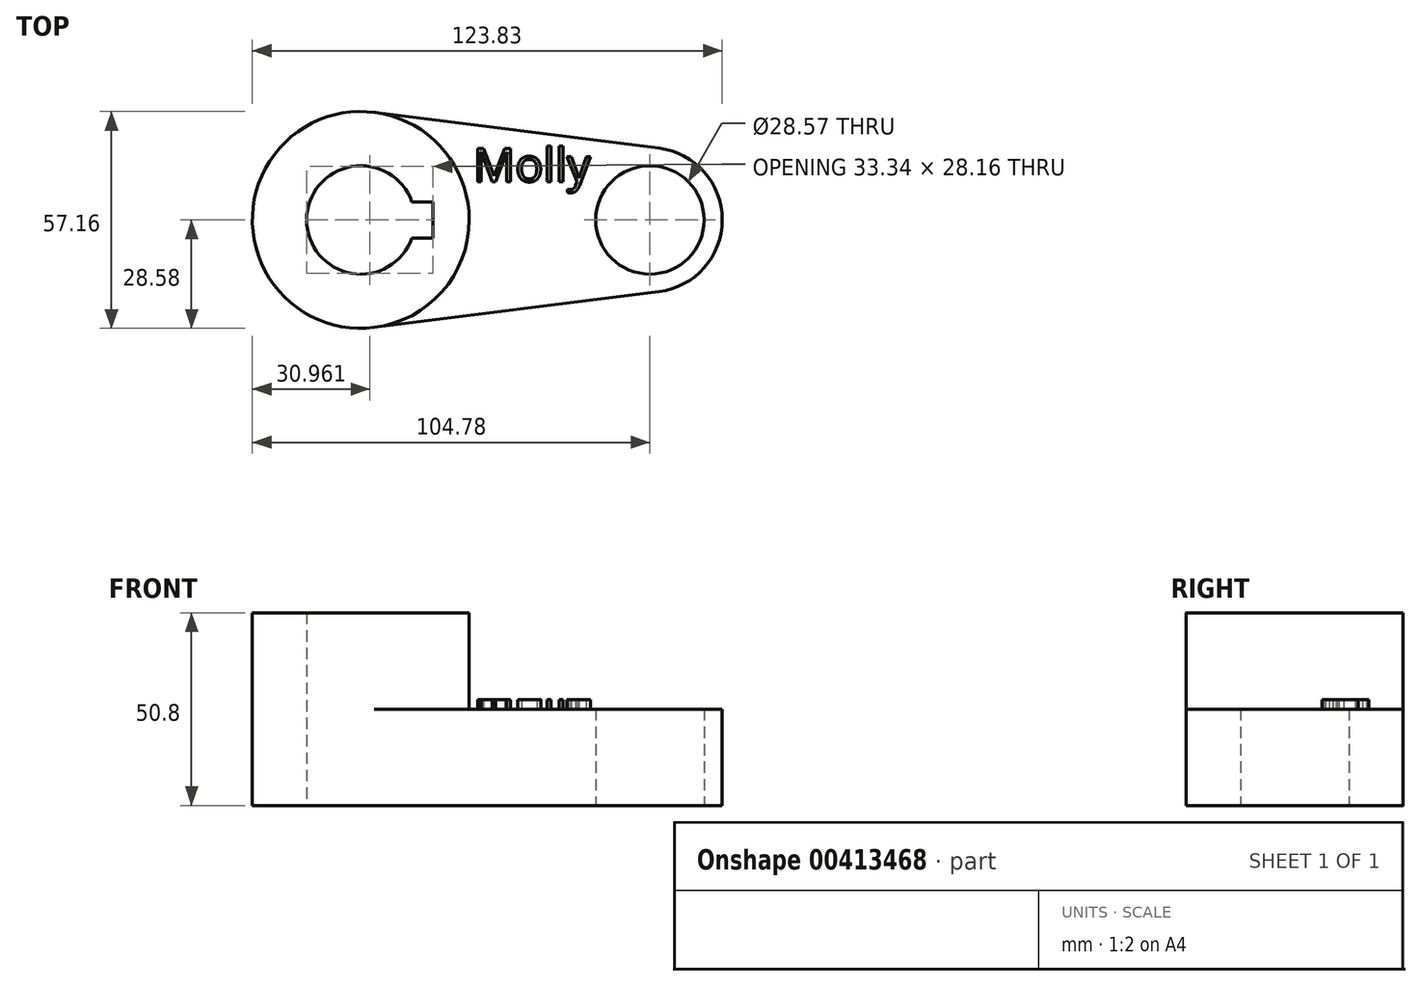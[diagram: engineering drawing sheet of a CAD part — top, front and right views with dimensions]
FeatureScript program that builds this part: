
annotation { "Feature Type Name" : "Feature", "Feature Type Description" : "" }
export const myFeature = defineFeature(function(context is Context, id is Id, definition is map)
    precondition{}
    {
        {
            var Q0;
            Q0=qCreatedBy(makeId("Top.planeOp"),FACE);
            var sketch = newSketch(context, id + "F0", { "sketchPlane" : qUnion([Q0])});
            skCircle(sketch, "E0", {"center": v(0, 0) * mm, "radius": 28.58 * mm});
            skCircle(sketch, "E1", {"center": v(76.2, 0) * mm, "radius": 19.05 * mm});
            skLineSegment(sketch, "E2", {"start": v(3.57, 28.35) * mm, "end": v(78.58, 18.9) * mm});
            skLineSegment(sketch, "E3", {"start": v(3.57, -28.35) * mm, "end": v(78.58, -18.9) * mm});
            skCircle(sketch, "E4", {"center": v(0, 0) * mm, "radius": 14.29 * mm});
            skCircle(sketch, "E5", {"center": v(76.2, 0) * mm, "radius": 14.29 * mm});
            skLineSegment(sketch, "E6.bottom", {"start": v(-19.05, -4.76) * mm, "end": v(19.05, -4.76) * mm});
            skLineSegment(sketch, "E6.top", {"start": v(-19.05, 4.76) * mm, "end": v(19.05, 4.76) * mm});
            skLineSegment(sketch, "E6.left", {"start": v(-19.05, -4.76) * mm, "end": v(-19.05, 4.76) * mm});
            skLineSegment(sketch, "E6.right", {"start": v(19.05, -4.76) * mm, "end": v(19.05, 4.76) * mm});
            skSolve(sketch);
        }
        {
            var Q0;
            {var subQ7=sQuery(id+"F0.wireOp",EDGE,"E6.left");Q0=makeQuery(id+"F0.imprint","IMPRINT",FACE,{"disambiguationData":[TD([[makeQuery(id+"F0.imprint","IMPRINT",EDGE,{"derivedFrom":subQ7}),1.0]])]});}
            var Q1;
            {var subQ5=sQuery(id+"F0.wireOp",EDGE,"E6.left");Q1=makeQuery(id+"F0.imprint","IMPRINT",FACE,{"disambiguationData":[TD([[makeQuery(id+"F0.imprint","IMPRINT",EDGE,{"derivedFrom":subQ5}),-1.0]])]});}
            var Q2;
            {var subQ0=sQuery(id+"F0.wireOp",EDGE,"E2");Q2=makeQuery(id+"F0.imprint","IMPRINT",FACE,{"disambiguationData":[TD([[makeQuery(id+"F0.imprint","IMPRINT",EDGE,{"derivedFrom":subQ0}),-1.0]])]});}
            var Q3;
            Q3=makeQuery(id+"F0.imprint","IMPRINT",FACE,{"disambiguationData":[TD([[makeQuery(id+"F0.imprint","IMPRINT",EDGE,{"derivedFrom":sQuery(id+"F0.wireOp",EDGE,"E5")}),-1.0]])]});
            extrude(context, id + "F1", {"entities" : qUnion([Q0, Q1, Q2, Q3]), "depth" : 25.4 * mm});
        }
        {
            var Q0;
            {var subQ7=sQuery(id+"F0.wireOp",EDGE,"E6.left");Q0=makeQuery(id+"F0.imprint","IMPRINT",FACE,{"disambiguationData":[TD([[makeQuery(id+"F0.imprint","IMPRINT",EDGE,{"derivedFrom":subQ7}),1.0]])]});}
            var Q1;
            {var subQ5=sQuery(id+"F0.wireOp",EDGE,"E6.left");Q1=makeQuery(id+"F0.imprint","IMPRINT",FACE,{"disambiguationData":[TD([[makeQuery(id+"F0.imprint","IMPRINT",EDGE,{"derivedFrom":subQ5}),-1.0]])]});}
            extrude(context, id + "F2", {"entities" : qUnion([Q0, Q1]), "operationType" : NewBodyOperationType.ADD, "depth" : 50.8 * mm});
        }
        {
            var Q0;
            Q0=makeQuery(id+"F1.opExtrude","CAP_FACE",FACE,{"disambiguationData":[OSD([sQuery(id+"F0.wireOp",EDGE,"E0"),sQuery(id+"F0.wireOp",EDGE,"E1"),sQuery(id+"F0.wireOp",EDGE,"E2"),sQuery(id+"F0.wireOp",EDGE,"E3"),sQuery(id+"F0.wireOp",EDGE,"E4"),sQuery(id+"F0.wireOp",EDGE,"E5"),sQuery(id+"F0.wireOp",EDGE,"E6.bottom"),sQuery(id+"F0.wireOp",EDGE,"E6.top"),sQuery(id+"F0.wireOp",EDGE,"E6.right")])],"isStart":false});
            var sketch = newSketch(context, id + "F3", { "sketchPlane" : qUnion([Q0])});
            skText(sketch, "E7", { "text": "Molly", "fontName": "OpenSans-Regular.ttf"});
            const initialGuessF3  = {"E7": [0.02957, 0.0101, 1, 0, 0.00886]};
            skSetInitialGuess(sketch, initialGuessF3);
            skSolve(sketch);
        }
        {
            var Q0;
            Q0 = qSketchRegion(id + "F3", true);
            extrude(context, id + "F4", {"entities" : qUnion([Q0]), "operationType" : NewBodyOperationType.ADD, "depth" : 2.54 * mm});
        }
    });
